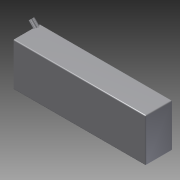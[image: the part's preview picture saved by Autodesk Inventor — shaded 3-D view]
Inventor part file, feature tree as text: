
AUTODESK INVENTOR PART (.ipt)
format: ipt  version: 2011 SP2 (Build 150309200, 309)  size: 123,392 bytes
history: native  units: mm
features: extrude x2, sketch x2, plane x1, fillet x1
ambient origin geometry x8: Origin, YZ Plane, XZ Plane, XY Plane, X Axis, Y Axis, Z Axis, Center Point
bodies: Solid1 (feature_tree)
feature tree (6):
  extrude  "Extrusion1"  Depth=28.0mm
  plane  "Work Plane1"
  extrude  "Extrusion2"  TaperAngle=135.0deg  [1 undecoded]
  fillet  "Fillet1"  Radius=3.0mm
  sketch  "Sketch1"  dims[d0=138.0mm d1=28.0mm]
  sketch  "Sketch2"  dims[d2=45.0mm d3=0.0mm d4=135.0deg d5=3.0mm d6=3.0mm d7=1.0mm d8=1.0mm d9=1.0mm d10=12.5mm d11=0.0mm d12=1.0mm]
note: 1 required parameter value undecoded (feature->parameter linkage not recoverable at this tier; creation-order binding heuristic only, values carry confidence <= 0.55)
